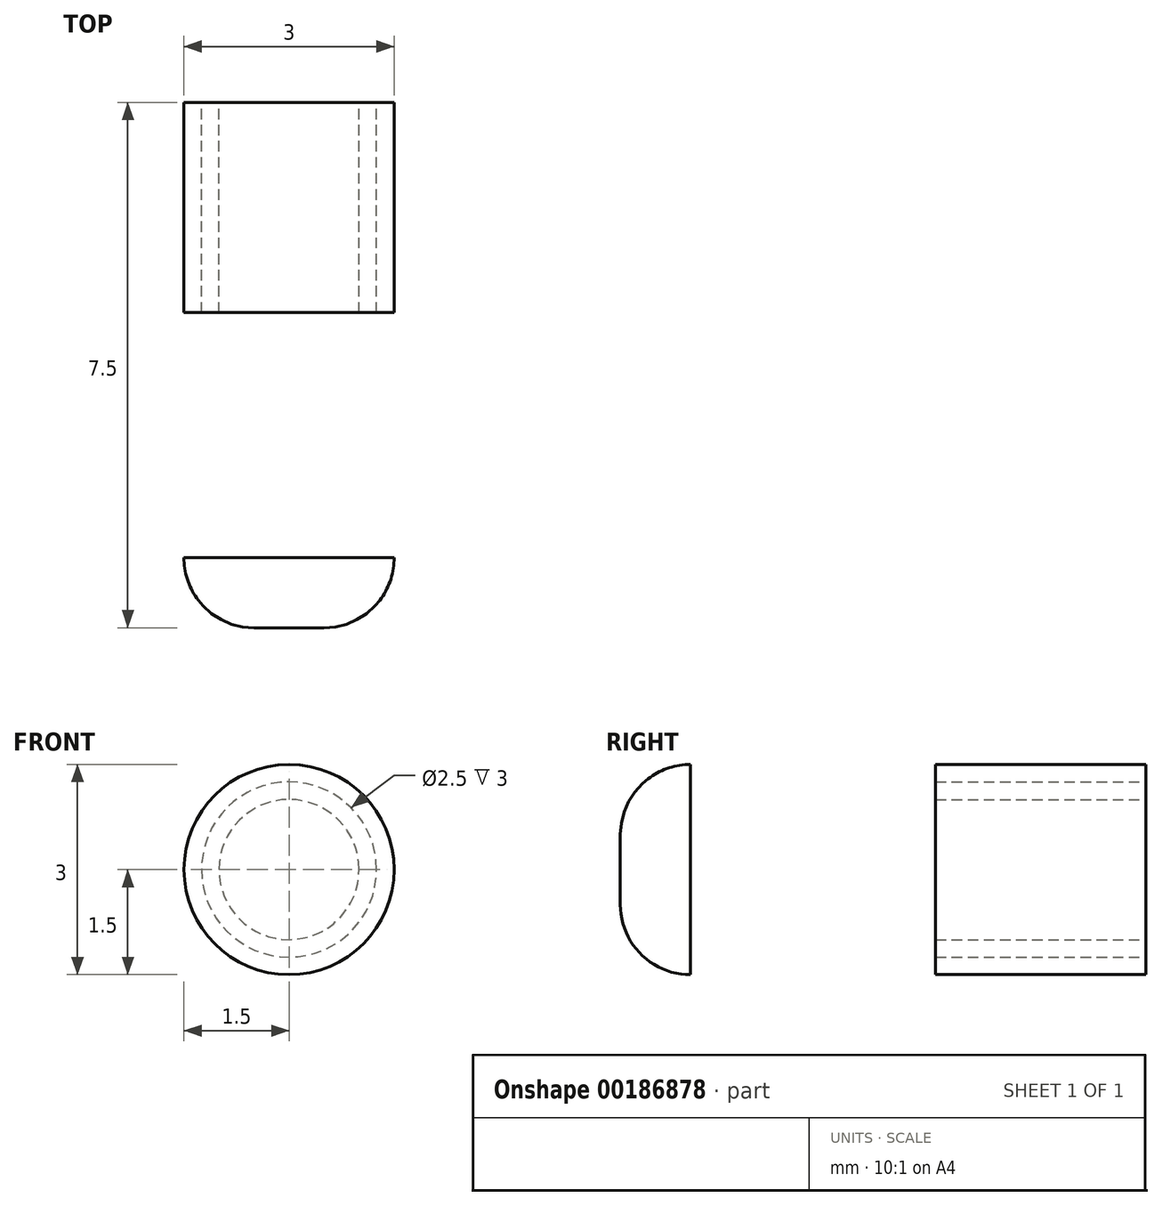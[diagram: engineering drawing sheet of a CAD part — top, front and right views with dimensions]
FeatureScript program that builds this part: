
annotation { "Feature Type Name" : "Feature", "Feature Type Description" : "" }
export const myFeature = defineFeature(function(context is Context, id is Id, definition is map)
    precondition{}
    {
        {
            var Q0;
            Q0=qCreatedBy(makeId("Front.planeOp"),FACE);
            var sketch = newSketch(context, id + "F0", { "sketchPlane" : qUnion([Q0])});
            skCircle(sketch, "E0", {"center": v(0, 0) * mm, "radius": 1.5 * mm});
            skCircle(sketch, "E1", {"center": v(0, 0) * mm, "radius": 1.25 * mm});
            skSolve(sketch);
        }
        {
            var Q0;
            Q0=qCreatedBy(makeId("Right.planeOp"),FACE);
            var sketch = newSketch(context, id + "F1", { "sketchPlane" : qUnion([Q0])});
            skFitSpline(sketch, "E2", {"points": [v(0, 0) * mm, v(32.86, -0.53) * mm, v(75.95, -7.96) * mm], "startDerivative": vector(65.78, 11.9) * mm, "endDerivative": vector(85.48, -26.55) * mm});
            skSolve(sketch);
        }
        {
            var Q0;
            Q0=qSketchRegion(id+"F0",true);
            var Q1;
            Q1=qConstructionFilter(qBodyType(qCreatedBy(id+"F1",EDGE),BodyType.WIRE),ConstructionObject.NO);
            sweep(context, id + "F2", {"profiles" : qUnion([Q0]), "path" : qUnion([Q1])});
        }
        {
            var Q0;
            Q0=qSketchRegion(id+"F0",true);
            extrude(context, id + "F3", {"entities" : qUnion([Q0]), "depth" : 3 * mm});
        }
        {
            var Q0;
            Q0=qCreatedBy(makeId("Front.planeOp"),FACE);
            var sketch = newSketch(context, id + "F4", { "sketchPlane" : qUnion([Q0])});
            skCircle(sketch, "E3", {"center": v(0, 0) * mm, "radius": 1 * mm});
            skSolve(sketch);
        }
        {
            var Q0;
            Q0=makeQuery(id+"F4.imprint","IMPRINT",FACE,{"disambiguationData":[TD([[makeQuery(id+"F4.imprint","IMPRINT",EDGE,{"derivedFrom":sQuery(id+"F4.wireOp",EDGE,"E3")}),1.0]])]});
            extrude(context, id + "F5", {"entities" : qUnion([Q0]), "depth" : 3 * mm});
        }
        {
            var Q0;
            Q0=qCreatedBy(makeId("Front.planeOp"),FACE);
            cPlane(context, id + "F6", {"entities" : qUnion([Q0]), "cplaneType" : CPlaneType.OFFSET, "offset" : 6.5 * mm, "width" : 152.4 * mm, "height" : 152.4 * mm});
        }
        {
            var Q0;
            Q0=qCreatedBy(id+"F6.planeOp",FACE);
            var sketch = newSketch(context, id + "F7", { "sketchPlane" : qUnion([Q0])});
            skCircle(sketch, "E4", {"center": v(0, 0) * mm, "radius": 1.5 * mm});
            skSolve(sketch);
        }
        {
            var Q0;
            Q0=qSketchRegion(id+"F7",true);
            extrude(context, id + "F8", {"entities" : qUnion([Q0]), "depth" : 1 * mm});
        }
        {
            var Q0;
            Q0=makeQuery(id+"F8.opExtrude","CAP_FACE",FACE,{"disambiguationData":[OSD([sQuery(id+"F7.wireOp",EDGE,"E4")])],"isStart":false});
            fillet(context, id + "F9", {"entities" : qUnion([Q0]), "radius" : 1 * mm, "tangentPropagation" : true, "allowEdgeOverflow" : false});
        }
        {
            var Q0;
            Q0=qCreatedBy(makeId("Front.planeOp"),FACE);
            var sketch = newSketch(context, id + "F10", { "sketchPlane" : qUnion([Q0])});
            skCircle(sketch, "E5", {"center": v(0, 0) * mm, "radius": 2.37 * mm});
            skSolve(sketch);
        }
        {
            var Q0;
            Q0=makeQuery(id+"F5.opExtrude","CAP_FACE",FACE,{"disambiguationData":[OSD([sQuery(id+"F4.wireOp",EDGE,"E3")])],"isStart":true});
            var Q1;
            Q1=qConstructionFilter(qBodyType(qCreatedBy(id+"F1",EDGE),BodyType.WIRE),ConstructionObject.NO);
            sweep(context, id + "F11", {"profiles" : qUnion([Q0]), "path" : qUnion([Q1])});
        }
        {
            var Q0;
            Q0=qSketchRegion(id+"F10",true);
            var Q1;
            Q1=qConstructionFilter(qBodyType(qCreatedBy(id+"F1",EDGE),BodyType.WIRE),ConstructionObject.NO);
            sweep(context, id + "F12", {"operationType" : NewBodyOperationType.REMOVE, "profiles" : qUnion([Q0]), "path" : qUnion([Q1])});
        }
    });
